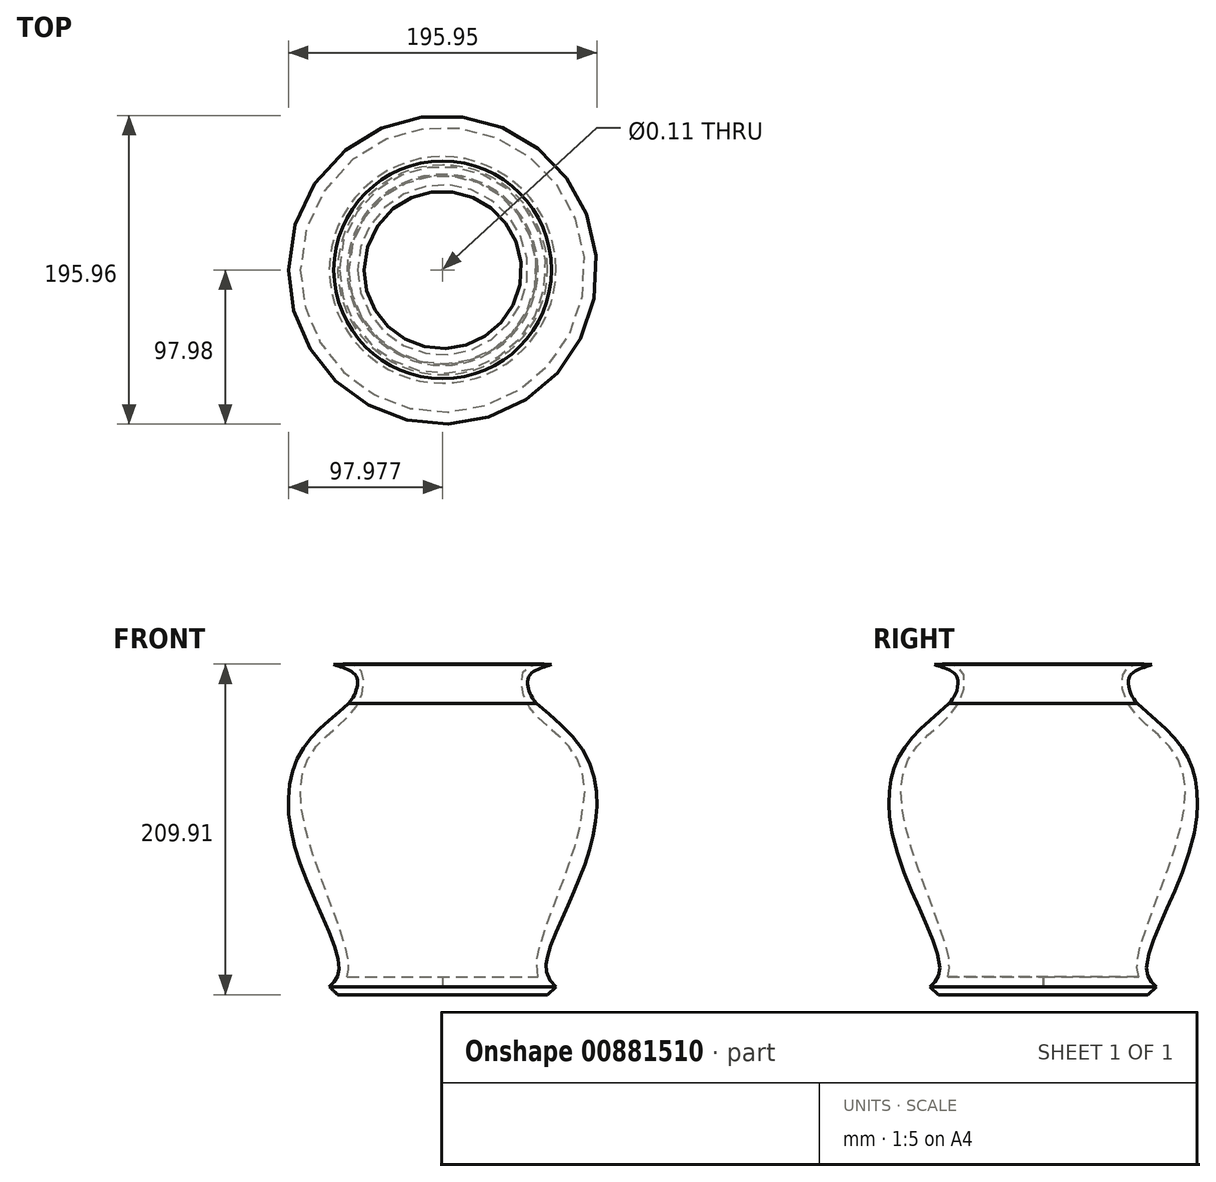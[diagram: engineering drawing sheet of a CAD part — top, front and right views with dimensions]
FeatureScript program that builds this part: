
annotation { "Feature Type Name" : "Feature", "Feature Type Description" : "" }
export const myFeature = defineFeature(function(context is Context, id is Id, definition is map)
    precondition{}
    {
        {
            var Q0;
            Q0=qCreatedBy(makeId("Front.planeOp"),FACE);
            var sketch = newSketch(context, id + "F0", { "sketchPlane" : qUnion([Q0])});
            skLineSegment(sketch, "E0", {"start": v(-53.46, 104.09) * mm, "end": v(-49.63, -98.88) * mm});
            skLineSegment(sketch, "E1", {"start": v(27.02, -105.36) * mm, "end": v(159.25, -105.36) * mm});
            skLineSegment(sketch, "E2", {"start": v(93.13, -97.97) * mm, "end": v(159.69, -97.97) * mm});
            skPoint(sketch, "E2.startSnap0", {"position": v(93.13, -105.36) * mm});
            skLineSegment(sketch, "E3", {"start": v(159.69, -97.97) * mm, "end": v(165.05, -92.95) * mm});
            skFitSpline(sketch, "E4", {"points": [v(165.05, -92.95) * mm, v(158.68, -80.55) * mm, v(185.82, -7.85) * mm, v(184.48, 53.46) * mm, v(152.88, 87.01) * mm], "startDerivative": vector(-70.3, 68.28) * mm, "endDerivative": vector(-138.64, 123.12) * mm});
            skFitSpline(sketch, "E5", {"points": [v(152.88, 87.01) * mm, v(147.93, 104.09) * mm, v(162.2, 111.75) * mm], "startDerivative": vector(-24.84, 23.97) * mm, "endDerivative": vector(30, 12.22) * mm});
            skLineSegment(sketch, "E6", {"start": v(93.13, -97.97) * mm, "end": v(93.13, -86.6) * mm});
            skLineSegment(sketch, "E7", {"start": v(93.13, -86.6) * mm, "end": v(153.7, -86.6) * mm});
            skFitSpline(sketch, "E8", {"points": [v(153.7, -86.6) * mm, v(153.7, -71.46) * mm, v(182.79, 20.58) * mm, v(171.63, 61.61) * mm, v(146.93, 86.72) * mm, v(145.33, 108.63) * mm, v(162.2, 111.75) * mm], "startDerivative": vector(-23.25, 101.09) * mm, "endDerivative": vector(169.11, -7.9) * mm});
            skSolve(sketch);
        }
        {
            var Q0;
            Q0=qCreatedBy(makeId("Front.planeOp"),FACE);
            var Q1;
            Q1=qCreatedBy(makeId("Front.planeOp"),FACE);
            var sketch = newSketch(context, id + "F1", { "sketchPlane" : qUnion([Q0, Q1])});
            skLineSegment(sketch, "E9", {"start": v(93.08, -105.8) * mm, "end": v(93.08, 125.95) * mm});
            skSolve(sketch);
        }
        {
            var Q0;
            Q0=makeQuery(id+"F0.imprint","IMPRINT",FACE,{"disambiguationData":[TD([[makeQuery(id+"F0.imprint","IMPRINT",EDGE,{"derivedFrom":sQuery(id+"F0.wireOp",EDGE,"E2")}),1.0]])]});
            var Q1;
            Q1=sQuery(id+"F1.wireOp",EDGE,"E9");
            revolve(context, id + "F2", {"surfaceOperationType" : NewSurfaceOperationType.NEW, "entities" : qUnion([Q0]), "axis" : qUnion([Q1]), "revolveType" : RevolveType.FULL});
        }
        {
            var Q0;
            Q0=qCreatedBy(makeId("Front.planeOp"),FACE);
            var sketch = newSketch(context, id + "F3", { "sketchPlane" : qUnion([Q0])});
            skFitSpline(sketch, "E10", {"points": [v(151.3, 68.57) * mm, v(173.55, 109.53) * mm, v(236.05, 101.76) * mm, v(240.29, 49.5) * mm, v(176.38, 0) * mm], "startDerivative": vector(53.33, 225.82) * mm, "endDerivative": vector(-270.43, -144.89) * mm});
            skSolve(sketch);
        }
        {
            var Q0;
            Q0=sQuery(id+"F3.wireOp",EDGE,"E10");
            var Q1;
            Q1=sQuery(id+"F3.wireOp",VERTEX,"E10.end");
            cPlane(context, id + "F4", {"entities" : qUnion([Q0, Q1]), "cplaneType" : CPlaneType.CURVE_POINT, "offset" : 25 * mm, "width" : 150 * mm, "height" : 150 * mm});
        }
    });
